# Revit family: Domotics-DomesticRanges-GEWISS-SYSTEM_PLATES_SUPPORT
name_source: partatom
category: Apparecchi elettrici
revit_build: Autodesk Revit 2016 (Build: 20161004_0715(x64)
units: mm (PartAtom-declared; Revit-internal decimal feet)

## family parameters
Basato su piano di lavoro = Sì
Condiviso = Sì
Mantenere orientamento annotazione = Sì
Punto di calcolo locali = Sì
Quota connettore circolare = Usa diametro
Sempre verticale = Sì
Taglio con vuoti quando caricato = No
Tipo di parte = Normale

## types (4) — shared parameters
Altezza foro = 45 mm  [stored 0.147638 ft]
Catalogue = DOMOTICS
Catalogue Range = SYSTEM - Special plates
Characteristics = Halogen free
Electrocod = 0121
IDF = bb9d2eda-35e4-4267-a821-72dd6e3d5cd1
IDT = fbf3fff7-ec7e-40b6-9c1d-e259ce2b67f9
Immagine tipo = <Nessuno>
Larghezza foro = 46 mm  [stored 0.150919 ft]
Larghezza supporto = 108 mm  [stored 0.354331 ft]
Materiale supporto = GEWISS - ACCIAIO SUPPORTO
Produttore = GEWISS S.p.A.
Prospetto di default = 1219 mm
SEO = Support
Technical sheet = https://www.gewiss.com
URL = https://www.gewiss.com
Version file RFA = 19.4

## per-type parameters (varying)
| type | Description: | Descrizione | EAN code | Fixing | Modello |
| GW24230 - 6 GANG SUPPORT FOR SYSTEM/VIRNA PLATE | 6 gang | 6 GANG SUPPORT FOR SYSTEM/VIRNA PLATE | 8011564055131 | 4 screws (included) | GW24230 |
| GW24202 - 4 GANG SUPPORT FOR SYSTEM PLATE | 4 gang | 4 GANG SUPPORT FOR SYSTEM PLATE | 8011564002265 | 2 screws (included) | GW24202 |
| GW24201 - 3 GANG SUPPORT FOR SYSTEM PLATE | 3 gang | 3 GANG SUPPORT FOR SYSTEM PLATE | 8011564002258 | 2 screws (included) | GW24201 |
| GW24262 - SYSTEM/VIRNA 2-GANG PLATE SUPPORT | 2 gang | SYSTEM/VIRNA 2-GANG PLATE SUPPORT | 8011564101272 | 2 screws (included) | GW24262 |

note: [stored X ft] marks values corroborated as IEEE doubles in the binary element streams (Revit-internal decimal feet)
